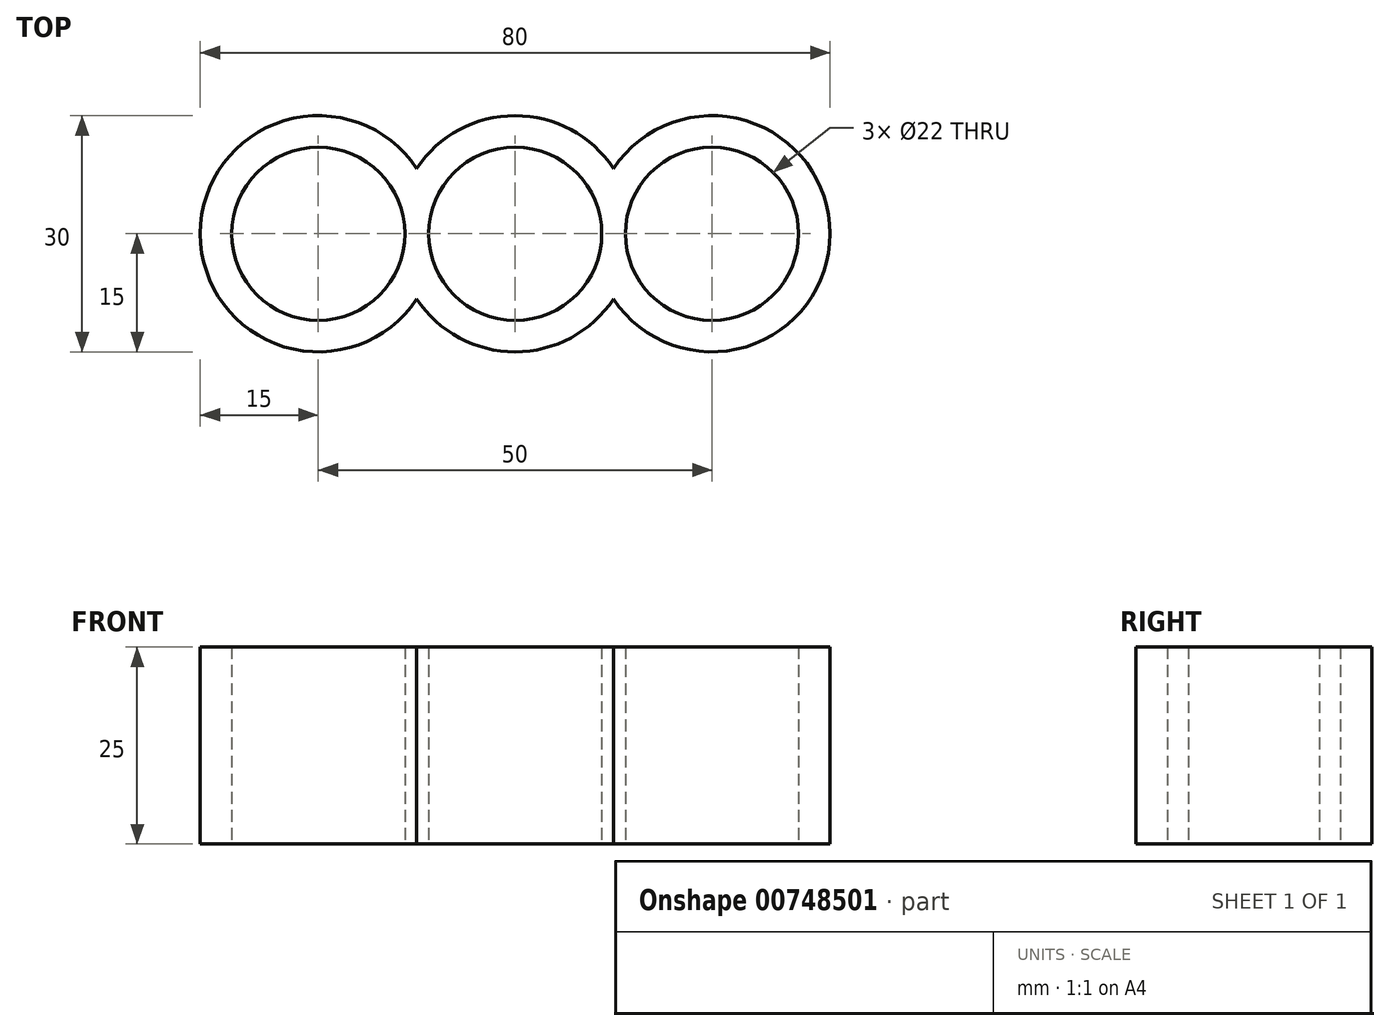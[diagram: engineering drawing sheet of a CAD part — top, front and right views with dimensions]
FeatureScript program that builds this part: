
annotation { "Feature Type Name" : "Feature", "Feature Type Description" : "" }
export const myFeature = defineFeature(function(context is Context, id is Id, definition is map)
    precondition{}
    {
        {
            var Q0;
            Q0=qCreatedBy(makeId("Top.planeOp"),FACE);
            var sketch = newSketch(context, id + "F0", { "sketchPlane" : qUnion([Q0])});
            skCircle(sketch, "E0", {"center": v(0, 0) * mm, "radius": 11 * mm});
            skArc(sketch, "E1", {"start": v(-12.5, -8.3) * mm, "mid": v(0, -15) * mm, "end": v(12.5, -8.3) * mm});
            skLineSegment(sketch, "E2", {"start": v(-11, 0) * mm, "end": v(-14, 0) * mm});
            skCircle(sketch, "E3", {"center": v(-25, 0) * mm, "radius": 11 * mm});
            skArc(sketch, "E4", {"start": v(-12.5, 8.3) * mm, "mid": v(-40, 0) * mm, "end": v(-12.5, -8.3) * mm});
            skCircle(sketch, "E5.MirrorC", {"center": v(25, 0) * mm, "radius": 11 * mm});
            skArc(sketch, "E6.MirrorCS", {"start": v(12.5, 8.3) * mm, "mid": v(40, 0) * mm, "end": v(12.5, -8.3) * mm});
            skArc(sketch, "E7.trimOffspring", {"start": v(12.5, 8.3) * mm, "mid": v(0, 15) * mm, "end": v(-12.5, 8.3) * mm});
            skSolve(sketch);
        }
        {
            var Q0;
            Q0 = qSketchRegion(id + "F0", true);
            extrude(context, id + "F1", {"entities" : qUnion([Q0]), "depth" : 25 * mm, "offsetDistance" : 25 * mm});
        }
    });
